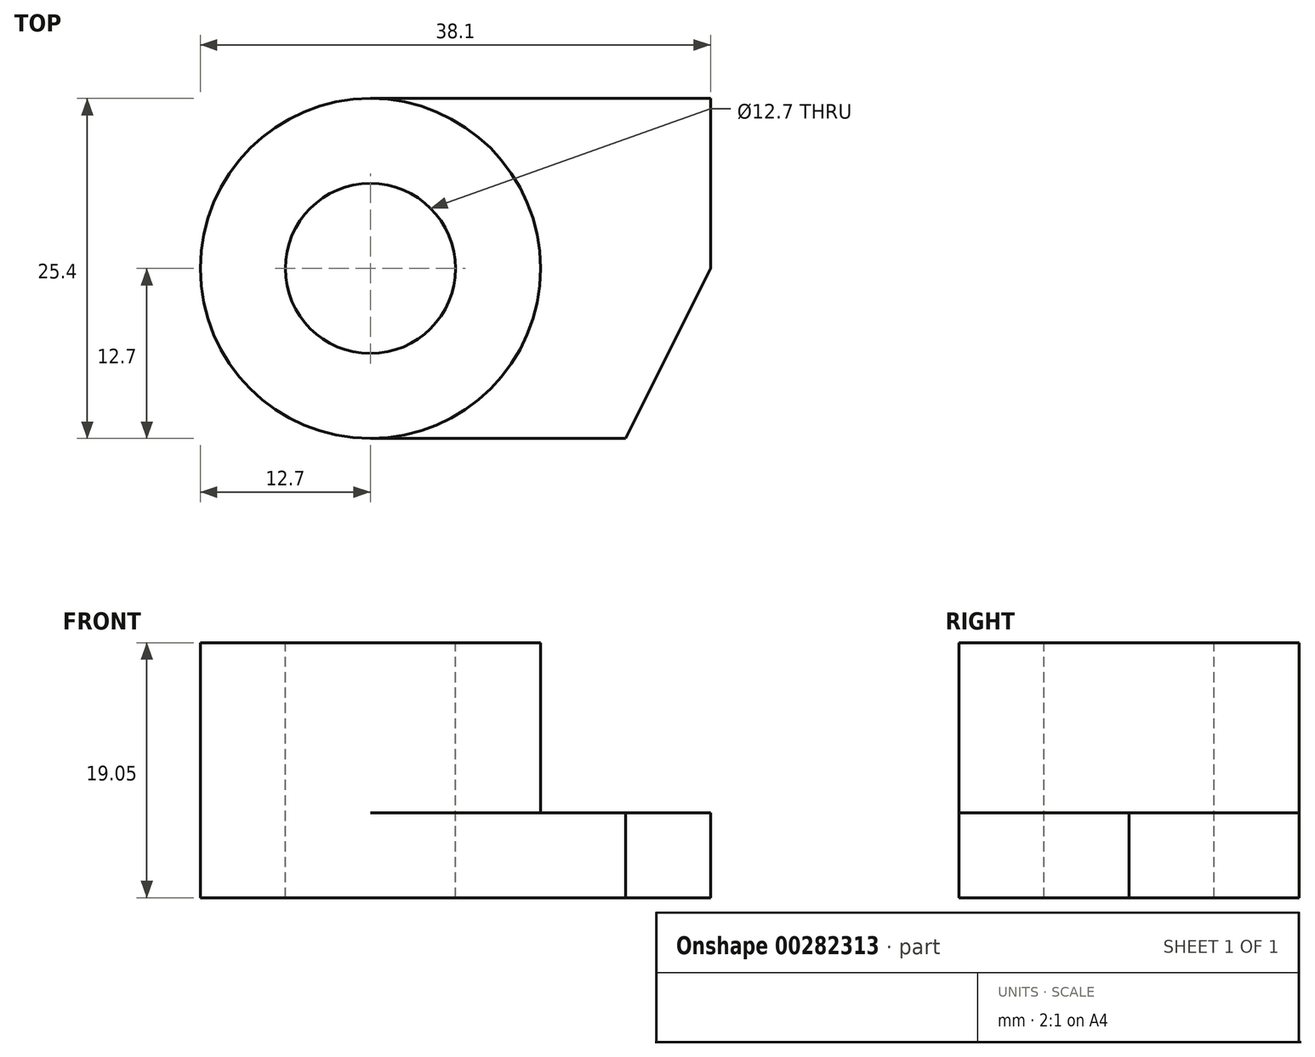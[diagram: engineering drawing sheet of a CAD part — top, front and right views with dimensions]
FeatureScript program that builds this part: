
annotation { "Feature Type Name" : "Feature", "Feature Type Description" : "" }
export const myFeature = defineFeature(function(context is Context, id is Id, definition is map)
    precondition{}
    {
        {
            var Q0;
            Q0=qCreatedBy(makeId("Top.planeOp"),FACE);
            var sketch = newSketch(context, id + "F0", { "sketchPlane" : qUnion([Q0])});
            skLineSegment(sketch, "E0", {"start": v(0, 0) * mm, "end": v(19.05, 0) * mm});
            skLineSegment(sketch, "E1", {"start": v(19.05, 0) * mm, "end": v(25.4, 12.7) * mm});
            skLineSegment(sketch, "E2", {"start": v(25.4, 12.7) * mm, "end": v(25.4, 25.4) * mm});
            skLineSegment(sketch, "E3", {"start": v(25.4, 25.4) * mm, "end": v(0, 25.4) * mm});
            skArc(sketch, "E4", {"start": v(0, 25.4) * mm, "mid": v(-12.7, 12.7) * mm, "end": v(0, 0) * mm});
            skSolve(sketch);
        }
        {
            var Q0;
            Q0=makeQuery(id+"F0.imprint","IMPRINT",FACE,{"disambiguationData":[TD([[makeQuery(id+"F0.imprint","IMPRINT",EDGE,{"derivedFrom":sQuery(id+"F0.wireOp",EDGE,"E0")}),1.0]])]});
            extrude(context, id + "F1", {"entities" : qUnion([Q0]), "depth" : 6.35 * mm});
        }
        {
            var Q0;
            Q0=makeQuery(id+"F1.opExtrude","CAP_FACE",FACE,{"disambiguationData":[OSD([sQuery(id+"F0.wireOp",EDGE,"E0"),sQuery(id+"F0.wireOp",EDGE,"E1"),sQuery(id+"F0.wireOp",EDGE,"E2"),sQuery(id+"F0.wireOp",EDGE,"E3"),sQuery(id+"F0.wireOp",EDGE,"E4")])],"isStart":false});
            var sketch = newSketch(context, id + "F2", { "sketchPlane" : qUnion([Q0])});
            skCircle(sketch, "E5", {"center": v(0, 12.7) * mm, "radius": 12.7 * mm});
            skSolve(sketch);
        }
        {
            var Q0;
            Q0 = qSketchRegion(id + "F2", true);
            extrude(context, id + "F3", {"entities" : qUnion([Q0]), "operationType" : NewBodyOperationType.ADD, "depth" : 12.7 * mm});
        }
        {
            var Q0;
            Q0=makeQuery(id+"F3.opExtrude","CAP_FACE",FACE,{"disambiguationData":[OSD([sQuery(id+"F2.wireOp",EDGE,"E5")])],"isStart":false});
            var sketch = newSketch(context, id + "F4", { "sketchPlane" : qUnion([Q0])});
            skCircle(sketch, "E6", {"center": v(0, 12.7) * mm, "radius": 6.35 * mm});
            skSolve(sketch);
        }
        {
            var Q0;
            Q0 = qSketchRegion(id + "F4", true);
            extrude(context, id + "F5", {"entities" : qUnion([Q0]), "operationType" : NewBodyOperationType.REMOVE, "oppositeDirection" : true, "depth" : 19.05 * mm});
        }
    });
